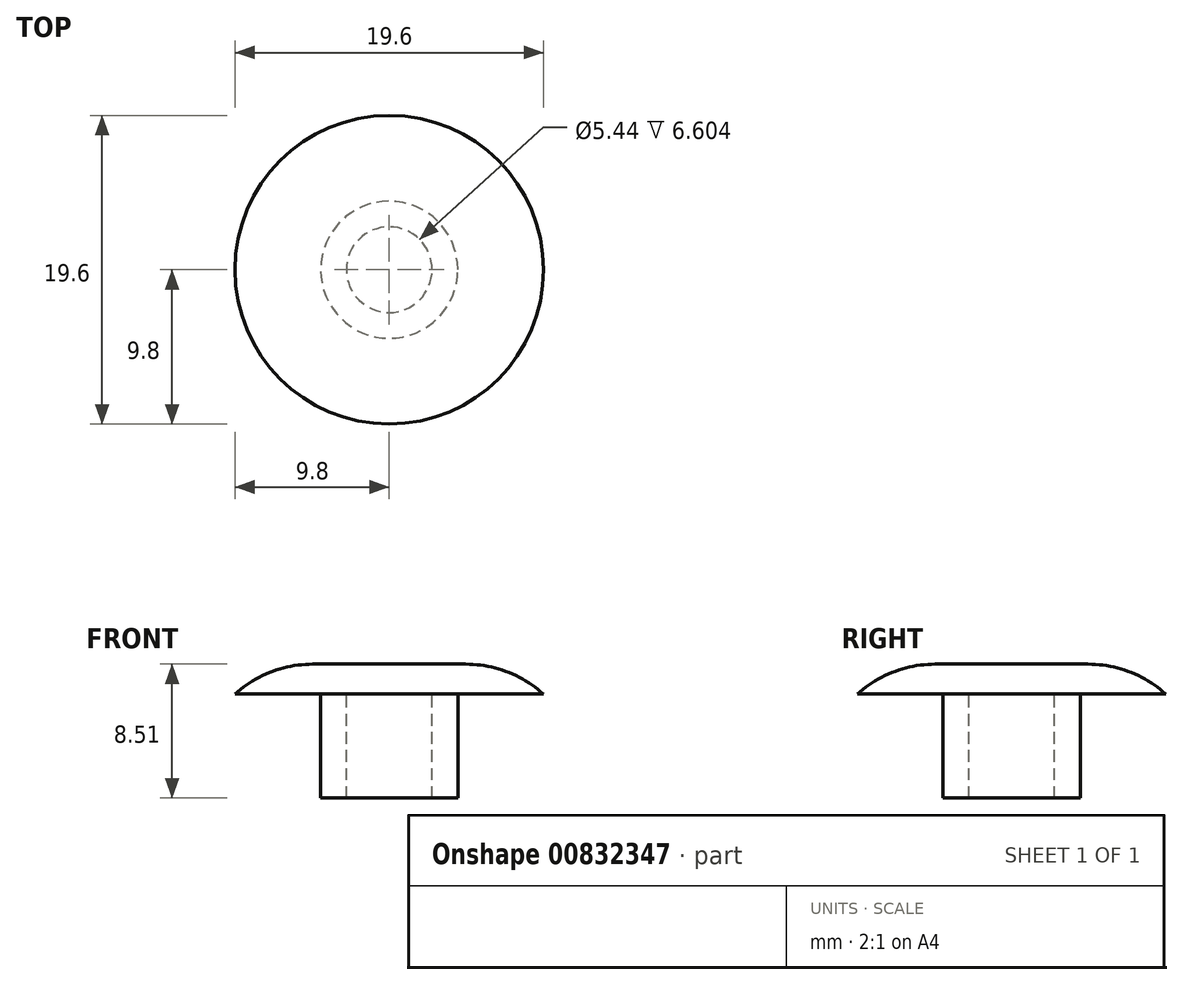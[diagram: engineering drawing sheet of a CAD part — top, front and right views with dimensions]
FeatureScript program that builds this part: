
annotation { "Feature Type Name" : "Feature", "Feature Type Description" : "" }
export const myFeature = defineFeature(function(context is Context, id is Id, definition is map)
    precondition{}
    {
        {
            var Q0;
            Q0=qCreatedBy(makeId("Top.planeOp"),FACE);
            var sketch = newSketch(context, id + "F0", { "sketchPlane" : qUnion([Q0])});
            skCircle(sketch, "E0", {"center": v(0, 0) * mm, "radius": 9.89 * mm, "construction": true});
            skCircle(sketch, "E1", {"center": v(0, 0) * mm, "radius": 4.36 * mm, "construction": true});
            skCircle(sketch, "E2", {"center": v(0, 0) * mm, "radius": 2.7 * mm, "construction": true});
            skCircle(sketch, "E3", {"center": v(0, 0) * mm, "radius": 9.8 * mm});
            skCircle(sketch, "E4", {"center": v(0, 0) * mm, "radius": 4.36 * mm});
            skCircle(sketch, "E5", {"center": v(0, 0) * mm, "radius": 2.72 * mm});
            skSolve(sketch);
        }
        {
            var Q0;
            Q0=makeQuery(id+"F0.imprint","IMPRINT",FACE,{"disambiguationData":[TD([[makeQuery(id+"F0.imprint","IMPRINT",EDGE,{"derivedFrom":sQuery(id+"F0.wireOp",EDGE,"E3")}),1.0]])]});
            extrude(context, id + "F1", {"entities" : qUnion([Q0]), "depth" : 1.9 * mm, "offsetDistance" : 25.4 * mm});
        }
        {
            var Q0;
            Q0=makeQuery(id+"F0.imprint","IMPRINT",FACE,{"disambiguationData":[TD([[makeQuery(id+"F0.imprint","IMPRINT",EDGE,{"derivedFrom":sQuery(id+"F0.wireOp",EDGE,"E5")}),1.0]])]});
            var Q1;
            Q1=makeQuery(id+"F0.imprint","IMPRINT",FACE,{"disambiguationData":[TD([[makeQuery(id+"F0.imprint","IMPRINT",EDGE,{"derivedFrom":sQuery(id+"F0.wireOp",EDGE,"E4")}),1.0]])]});
            extrude(context, id + "F2", {"entities" : qUnion([Q0, Q1]), "operationType" : NewBodyOperationType.ADD, "depth" : 1.9 * mm, "offsetDistance" : 25.4 * mm});
        }
        {
            var Q0;
            Q0=makeQuery(id+"F0.imprint","IMPRINT",FACE,{"disambiguationData":[TD([[makeQuery(id+"F0.imprint","IMPRINT",EDGE,{"derivedFrom":sQuery(id+"F0.wireOp",EDGE,"E4")}),1.0]])]});
            extrude(context, id + "F3", {"entities" : qUnion([Q0]), "operationType" : NewBodyOperationType.ADD, "oppositeDirection" : true, "depth" : 6.6 * mm, "offsetDistance" : 25.4 * mm});
        }
        {
            var Q0;
            Q0=makeQuery(id+"F1.opExtrude","CAP_EDGE",EDGE,{"disambiguationData":[OSD([sQuery(id+"F0.wireOp",EDGE,"E3")])],"isStart":false});
            fillet(context, id + "F4", {"entities" : qUnion([Q0]), "radius" : 7.36 * mm, "tangentPropagation" : true, "allowEdgeOverflow" : false});
        }
    });
